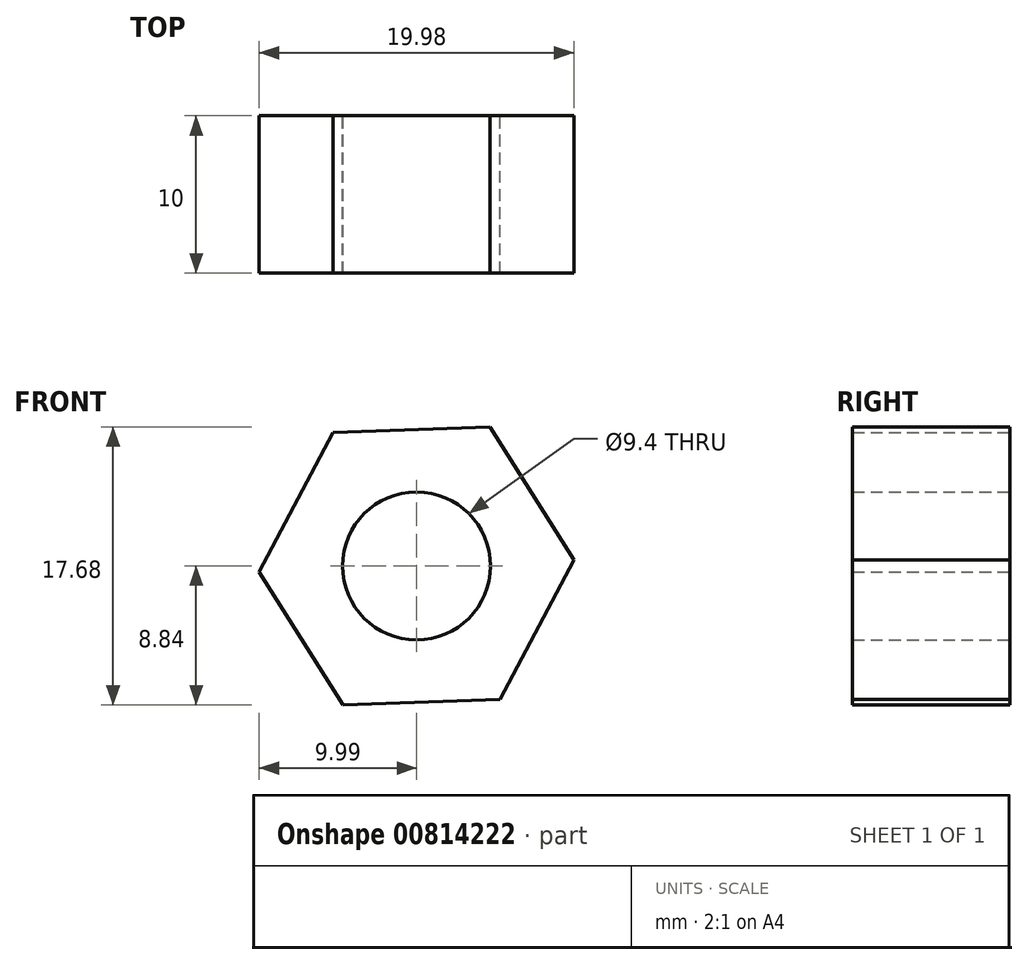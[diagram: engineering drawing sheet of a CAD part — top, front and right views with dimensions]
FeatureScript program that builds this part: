
annotation { "Feature Type Name" : "Feature", "Feature Type Description" : "" }
export const myFeature = defineFeature(function(context is Context, id is Id, definition is map)
    precondition{}
    {
        {
            var Q0;
            Q0=qCreatedBy(makeId("Front.planeOp"),FACE);
            var sketch = newSketch(context, id + "F0", { "sketchPlane" : qUnion([Q0])});
            skCircle(sketch, "E0.cCircle", {"center": v(0, 0) * mm, "radius": 8.66 * mm, "construction": true});
            skLineSegment(sketch, "E0.0", {"start": v(4.68, 8.84) * mm, "end": v(10, 0.37) * mm});
            skLineSegment(sketch, "E0.1", {"start": v(10, 0.37) * mm, "end": v(5.32, -8.47) * mm});
            skLineSegment(sketch, "E0.2", {"start": v(5.32, -8.47) * mm, "end": v(-4.68, -8.84) * mm});
            skLineSegment(sketch, "E0.3", {"start": v(-4.68, -8.84) * mm, "end": v(-10, -0.37) * mm});
            skLineSegment(sketch, "E0.4", {"start": v(-10, -0.37) * mm, "end": v(-5.32, 8.47) * mm});
            skLineSegment(sketch, "E0.5", {"start": v(-5.32, 8.47) * mm, "end": v(4.68, 8.84) * mm});
            skPoint(sketch, "E0.0.midPoint", {"position": v(7.34, 4.6) * mm});
            skCircle(sketch, "E1", {"center": v(0, 0) * mm, "radius": 4.7 * mm});
            skSolve(sketch);
        }
        {
            var Q0;
            Q0 = qSketchRegion(id + "F0", true);
            extrude(context, id + "F1", {"entities" : qUnion([Q0]), "depth" : 10 * mm, "offsetDistance" : 25 * mm});
        }
    });
